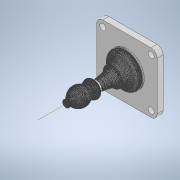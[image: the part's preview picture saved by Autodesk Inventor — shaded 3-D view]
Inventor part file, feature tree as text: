
AUTODESK INVENTOR PART (.ipt)
format: ipt  version: 2022 (Build 260153000, 153)  size: 20,253,184 bytes
history: native  units: mm
features: other x5, sketch x2, move_body x1, extrude x1, chamfer x1, revolve x1, projected_geometry x1
ambient origin geometry x8: Origin, YZ Plane, XZ Plane, XY Plane, X Axis, Y Axis, Z Axis, Center Point
bodies: Solid2 (feature_tree), Solid3 (feature_tree), Solid1 (feature_tree)
feature tree (12):
  other  "Queen Mold.ipt"
  other  "MeshFeature1"
  move_body  "Move Body1"
  extrude  "Extrusion1"  Depth=4.0mm
  chamfer  "Chamfer1"  Distance=4.0mm
  revolve  "Revolution1"  Angle=45.0deg
  other  "Solid2::Queen Mold.ipt"
  other  "TaggingFeature1"
  other  "Work Axis1"
  sketch  "Sketch1"  dims[d0=10.0mm d1=-100.248mm d2=2516.89mm d3=-1.844134mm d4=4.0mm d5=0.0mm]
  projected_geometry  "Projected Loop1"
  sketch  "Sketch2"  dims[d6=1.0mm d7=2.0mm d8=45.0deg d9=45.0deg d10=90.0deg]
